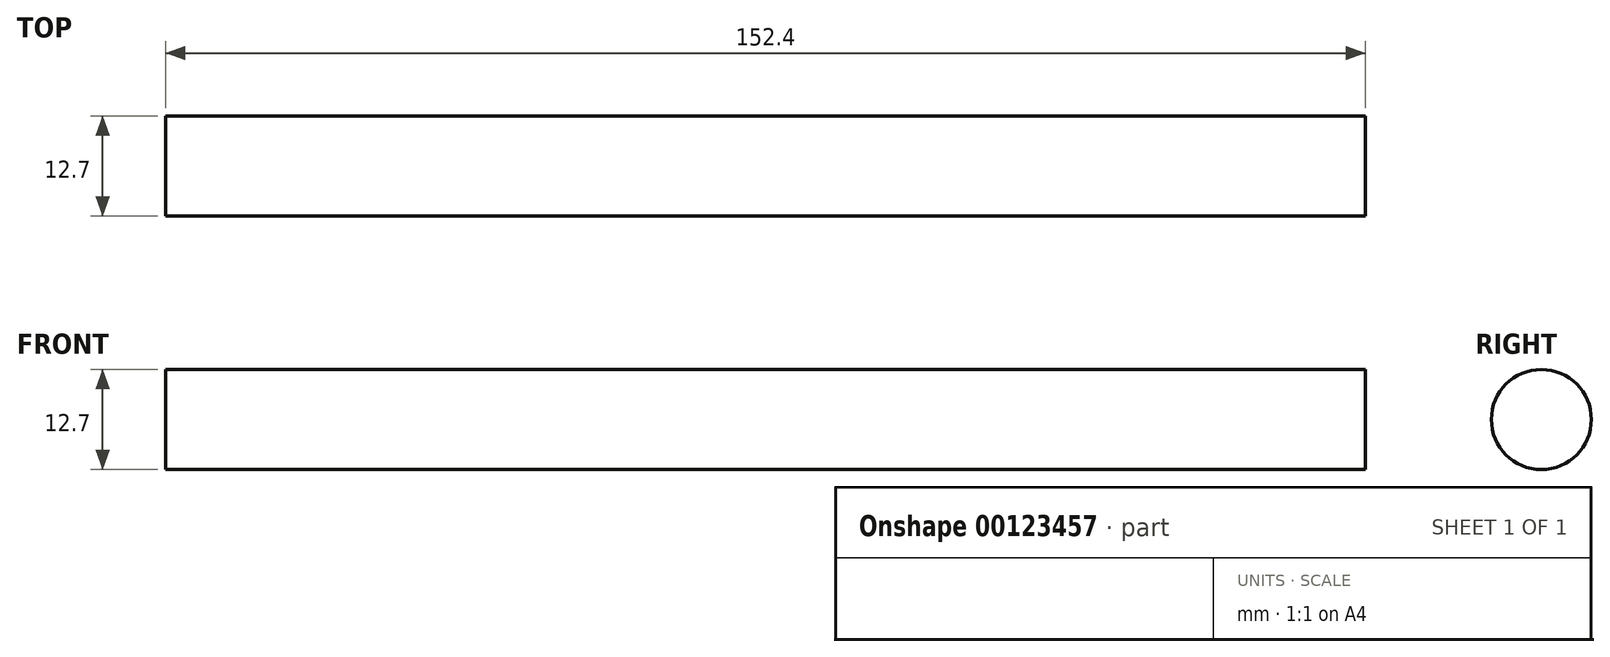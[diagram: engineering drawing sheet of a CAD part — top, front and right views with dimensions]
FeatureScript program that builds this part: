
annotation { "Feature Type Name" : "Feature", "Feature Type Description" : "" }
export const myFeature = defineFeature(function(context is Context, id is Id, definition is map)
    precondition{}
    {
        {
            var Q0;
            Q0=qCreatedBy(makeId("Right.planeOp"),FACE);
            var sketch = newSketch(context, id + "F0", { "sketchPlane" : qUnion([Q0])});
            skCircle(sketch, "E0", {"center": v(0, 0) * mm, "radius": 6.35 * mm});
            skSolve(sketch);
        }
        {
            var Q0;
            Q0 = qSketchRegion(id + "F0", true);
            extrude(context, id + "F1", {"entities" : qUnion([Q0]), "endBound" : BoundingType.SYMMETRIC, "depth" : 152.4 * mm});
        }
    });
